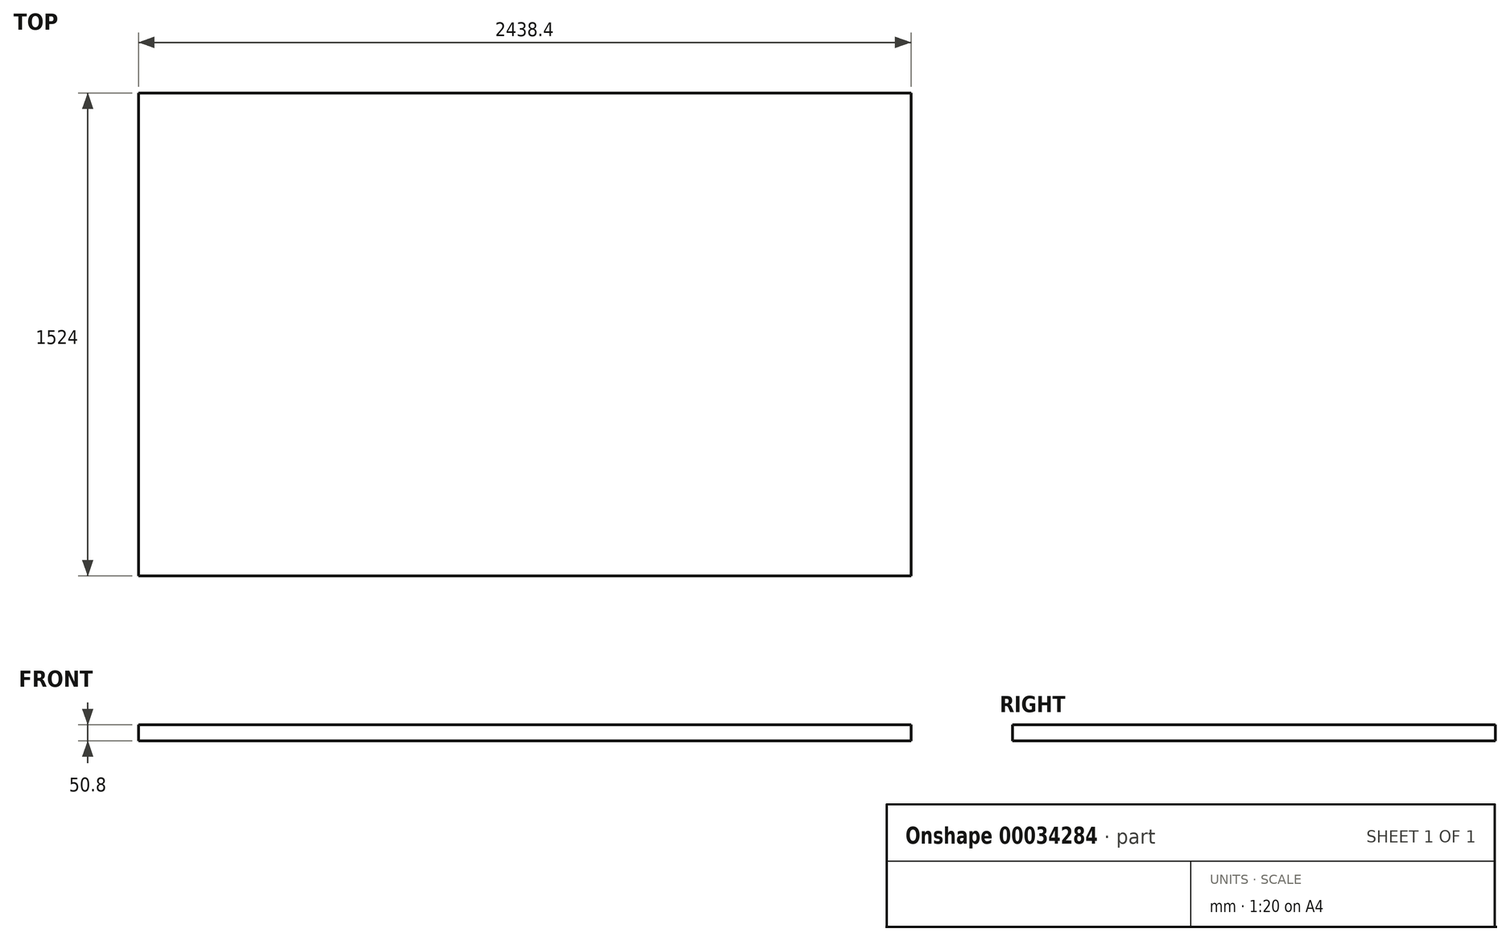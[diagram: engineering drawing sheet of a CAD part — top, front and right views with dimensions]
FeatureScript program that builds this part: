
annotation { "Feature Type Name" : "Feature", "Feature Type Description" : "" }
export const myFeature = defineFeature(function(context is Context, id is Id, definition is map)
    precondition{}
    {
        {
            var Q0;
            Q0=qCreatedBy(makeId("Top.planeOp"),FACE);
            var sketch = newSketch(context, id + "F0", { "sketchPlane" : qUnion([Q0])});
            skLineSegment(sketch, "E0.bottom", {"start": v(0, 0) * mm, "end": v(2438.4, 0) * mm});
            skLineSegment(sketch, "E0.top", {"start": v(0, 1524) * mm, "end": v(2438.4, 1524) * mm});
            skLineSegment(sketch, "E0.left", {"start": v(0, 0) * mm, "end": v(0, 1524) * mm});
            skLineSegment(sketch, "E0.right", {"start": v(2438.4, 0) * mm, "end": v(2438.4, 1524) * mm});
            skSolve(sketch);
        }
        {
            var Q0;
            Q0=makeQuery(id+"F0.imprint","IMPRINT",FACE,{"disambiguationData":[TD([[makeQuery(id+"F0.imprint","IMPRINT",EDGE,{"derivedFrom":sQuery(id+"F0.wireOp",EDGE,"E0.bottom")}),1.0]])]});
            extrude(context, id + "F1", {"entities" : qUnion([Q0]), "depth" : 50.8 * mm});
        }
    });
